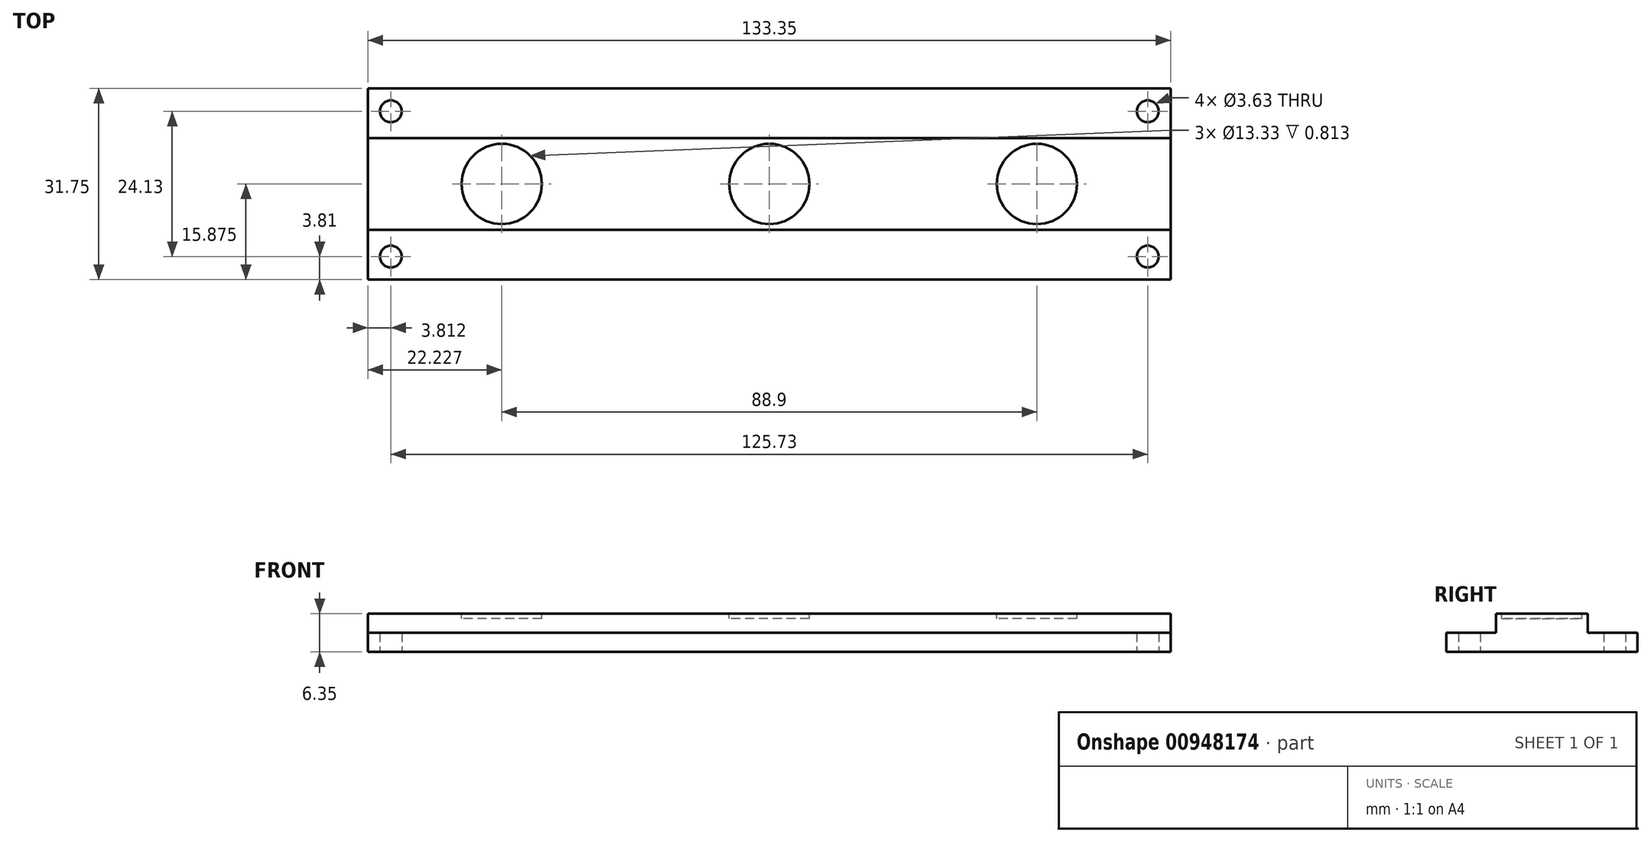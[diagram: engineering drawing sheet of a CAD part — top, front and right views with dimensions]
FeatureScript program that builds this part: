
annotation { "Feature Type Name" : "Feature", "Feature Type Description" : "" }
export const myFeature = defineFeature(function(context is Context, id is Id, definition is map)
    precondition{}
    {
        {
            var Q0;
            Q0=qCreatedBy(makeId("Top.planeOp"),FACE);
            var sketch = newSketch(context, id + "F0", { "sketchPlane" : qUnion([Q0])});
            skLineSegment(sketch, "E0.bottom", {"start": v(51.88, 0) * mm, "end": v(-81.47, 0) * mm});
            skLineSegment(sketch, "E0.top", {"start": v(51.88, -31.75) * mm, "end": v(-81.47, -31.75) * mm});
            skLineSegment(sketch, "E0.left", {"start": v(51.88, 0) * mm, "end": v(51.88, -31.75) * mm});
            skLineSegment(sketch, "E0.right", {"start": v(-81.47, 0) * mm, "end": v(-81.47, -31.75) * mm});
            skCircle(sketch, "E1", {"center": v(-77.66, -27.94) * mm, "radius": 1.82 * mm});
            skLineSegment(sketch, "E2", {"start": v(-81.47, -15.88) * mm, "end": v(51.88, -15.88) * mm, "construction": true});
            skLineSegment(sketch, "E3", {"start": v(-14.8, -31.75) * mm, "end": v(-14.8, 0) * mm, "construction": true});
            skCircle(sketch, "E4.MirrorC", {"center": v(-77.66, -3.81) * mm, "radius": 1.82 * mm});
            skCircle(sketch, "E5.MirrorC", {"center": v(48.07, -27.94) * mm, "radius": 1.82 * mm});
            skCircle(sketch, "E6.MirrorC", {"center": v(48.07, -3.8) * mm, "radius": 1.82 * mm});
            skLineSegment(sketch, "E7.left", {"start": v(-81.47, -8.22) * mm, "end": v(-81.47, -24.11) * mm});
            skLineSegment(sketch, "E7.right", {"start": v(51.88, -8.22) * mm, "end": v(51.88, -24.11) * mm});
            skSolve(sketch);
        }
        {
            var Q0;
            Q0=makeQuery(id+"F0.imprint","IMPRINT",FACE,{"disambiguationData":[TD([[makeQuery(id+"F0.imprint","IMPRINT",EDGE,{"derivedFrom":sQuery(id+"F0.wireOp",EDGE,"E0.bottom")}),1.0]])]});
            extrude(context, id + "F1", {"entities" : qUnion([Q0]), "depth" : 3.17 * mm, "offsetDistance" : 25.4 * mm});
        }
        {
            var Q0;
            Q0=makeQuery(id+"F1.opExtrude","CAP_FACE",FACE,{"disambiguationData":[OSD([sQuery(id+"F0.wireOp",EDGE,"E0.bottom"),sQuery(id+"F0.wireOp",EDGE,"E0.top"),sQuery(id+"F0.wireOp",EDGE,"E0.left"),sQuery(id+"F0.wireOp",EDGE,"E0.right"),sQuery(id+"F0.wireOp",EDGE,"E1"),sQuery(id+"F0.wireOp",EDGE,"E4.MirrorC"),sQuery(id+"F0.wireOp",EDGE,"E5.MirrorC"),sQuery(id+"F0.wireOp",EDGE,"E6.MirrorC"),sQuery(id+"F0.wireOp",EDGE,"E7.left"),sQuery(id+"F0.wireOp",EDGE,"E7.right")])],"isStart":false});
            var sketch = newSketch(context, id + "F2", { "sketchPlane" : qUnion([Q0])});
            skLineSegment(sketch, "E8", {"start": v(-81.47, 0) * mm, "end": v(51.88, -31.75) * mm, "construction": true});
            skLineSegment(sketch, "E9", {"start": v(-81.47, -31.75) * mm, "end": v(51.88, 0) * mm, "construction": true});
            skLineSegment(sketch, "E10.bottom", {"start": v(51.88, -23.5) * mm, "end": v(-81.47, -23.5) * mm});
            skLineSegment(sketch, "E10.top", {"start": v(51.88, -8.26) * mm, "end": v(-81.47, -8.26) * mm});
            skLineSegment(sketch, "E10.left", {"start": v(51.88, -23.5) * mm, "end": v(51.88, -8.26) * mm});
            skLineSegment(sketch, "E10.right", {"start": v(-81.47, -23.5) * mm, "end": v(-81.47, -8.26) * mm});
            skPoint(sketch, "E10.middle", {"position": v(-14.8, -15.88) * mm});
            skSolve(sketch);
        }
        {
            var Q0;
            Q0=makeQuery(id+"F2.imprint","IMPRINT",FACE,{"disambiguationData":[TD([[makeQuery(id+"F2.imprint","IMPRINT",EDGE,{"derivedFrom":sQuery(id+"F2.wireOp",EDGE,"E10.bottom")}),-1.0]])]});
            extrude(context, id + "F3", {"entities" : qUnion([Q0]), "operationType" : NewBodyOperationType.ADD, "depth" : 3.17 * mm, "offsetDistance" : 25.4 * mm});
        }
        {
            var Q0;
            Q0=makeQuery(id+"F3.opExtrude","CAP_FACE",FACE,{"disambiguationData":[OSD([sQuery(id+"F2.wireOp",EDGE,"E10.bottom"),sQuery(id+"F2.wireOp",EDGE,"E10.top"),sQuery(id+"F2.wireOp",EDGE,"E10.left"),sQuery(id+"F2.wireOp",EDGE,"E10.right")])],"isStart":false});
            var sketch = newSketch(context, id + "F4", { "sketchPlane" : qUnion([Q0])});
            skLineSegment(sketch, "E11", {"start": v(-81.47, -15.88) * mm, "end": v(51.88, -15.88) * mm, "construction": true});
            skLineSegment(sketch, "E12", {"start": v(-14.8, -8.26) * mm, "end": v(-14.8, -23.5) * mm, "construction": true});
            skCircle(sketch, "E13", {"center": v(-14.8, -15.88) * mm, "radius": 6.67 * mm});
            skCircle(sketch, "E14", {"center": v(29.66, -15.88) * mm, "radius": 6.67 * mm});
            skCircle(sketch, "E15", {"center": v(-59.24, -15.88) * mm, "radius": 6.67 * mm});
            skSolve(sketch);
        }
        {
            var Q0;
            Q0=makeQuery(id+"F4.imprint","IMPRINT",FACE,{"disambiguationData":[TD([[makeQuery(id+"F4.imprint","IMPRINT",EDGE,{"derivedFrom":sQuery(id+"F4.wireOp",EDGE,"E15")}),1.0]])]});
            var Q1;
            Q1=makeQuery(id+"F4.imprint","IMPRINT",FACE,{"disambiguationData":[TD([[makeQuery(id+"F4.imprint","IMPRINT",EDGE,{"derivedFrom":sQuery(id+"F4.wireOp",EDGE,"E13")}),1.0]])]});
            var Q2;
            Q2=makeQuery(id+"F4.imprint","IMPRINT",FACE,{"disambiguationData":[TD([[makeQuery(id+"F4.imprint","IMPRINT",EDGE,{"derivedFrom":sQuery(id+"F4.wireOp",EDGE,"E14")}),1.0]])]});
            extrude(context, id + "F5", {"entities" : qUnion([Q0, Q1, Q2]), "operationType" : NewBodyOperationType.REMOVE, "oppositeDirection" : true, "depth" : 0.81 * mm, "offsetDistance" : 25.4 * mm});
        }
    });
